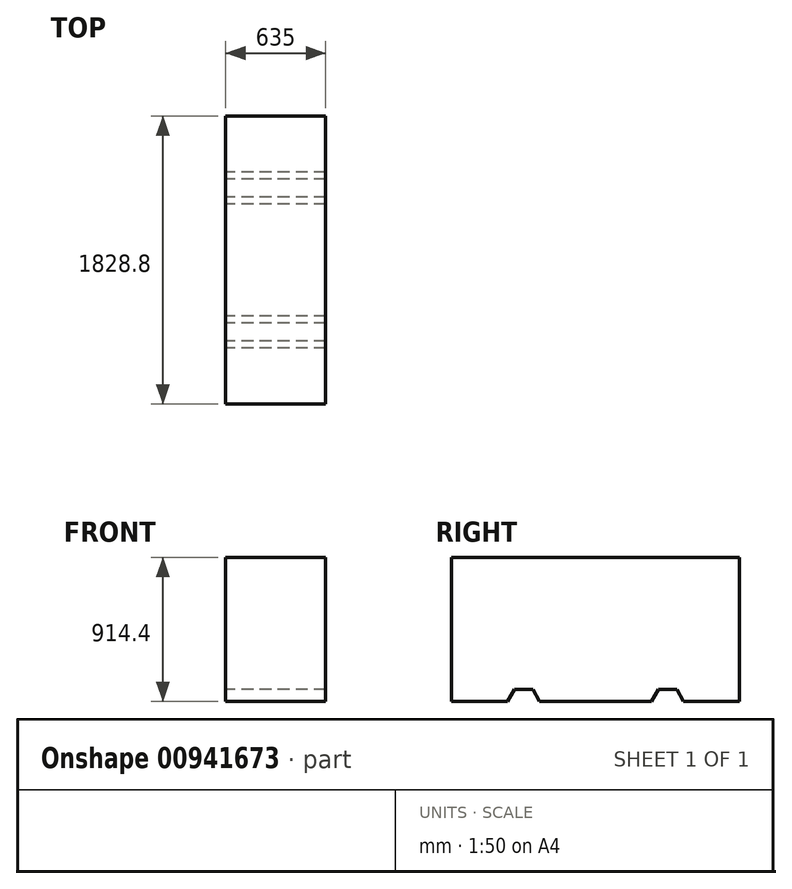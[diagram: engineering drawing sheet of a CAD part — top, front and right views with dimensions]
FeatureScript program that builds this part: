
annotation { "Feature Type Name" : "Feature", "Feature Type Description" : "" }
export const myFeature = defineFeature(function(context is Context, id is Id, definition is map)
    precondition{}
    {
        {
            var Q0;
            Q0=qCreatedBy(makeId("Right.planeOp"),FACE);
            var sketch = newSketch(context, id + "F0", { "sketchPlane" : qUnion([Q0])});
            skLineSegment(sketch, "E0.top", {"start": v(914.4, 457.2) * mm, "end": v(-914.4, 457.2) * mm});
            skLineSegment(sketch, "E0.left", {"start": v(914.4, -457.2) * mm, "end": v(914.4, 457.2) * mm});
            skLineSegment(sketch, "E0.right", {"start": v(-914.4, -457.2) * mm, "end": v(-914.4, 457.2) * mm});
            skPoint(sketch, "E0.middle", {"position": v(0, 0) * mm});
            skLineSegment(sketch, "E1", {"start": v(0, 607.57) * mm, "end": v(0, -605.26) * mm, "construction": true});
            skLineSegment(sketch, "E2", {"start": v(-457.2, 606.77) * mm, "end": v(-457.2, -606.07) * mm, "construction": true});
            skLineSegment(sketch, "E3", {"start": v(457.2, 704.09) * mm, "end": v(457.2, -508.75) * mm, "construction": true});
            skLineSegment(sketch, "E4", {"start": v(-914.4, -457.2) * mm, "end": v(-558.8, -457.2) * mm});
            skLineSegment(sketch, "E5", {"start": v(-558.8, -457.2) * mm, "end": v(-514.8, -381) * mm});
            skLineSegment(sketch, "E6", {"start": v(-514.8, -381) * mm, "end": v(-399.6, -381) * mm});
            skLineSegment(sketch, "E7", {"start": v(-399.6, -381) * mm, "end": v(-355.6, -457.2) * mm});
            skLineSegment(sketch, "E8", {"start": v(-355.6, -457.2) * mm, "end": v(355.6, -457.2) * mm});
            skLineSegment(sketch, "E9", {"start": v(355.6, -457.2) * mm, "end": v(399.6, -381) * mm});
            skLineSegment(sketch, "E10", {"start": v(399.6, -381) * mm, "end": v(514.8, -381) * mm});
            skLineSegment(sketch, "E11", {"start": v(514.8, -381) * mm, "end": v(558.8, -457.2) * mm});
            skLineSegment(sketch, "E12", {"start": v(558.8, -457.2) * mm, "end": v(914.4, -457.2) * mm});
            skSolve(sketch);
        }
        {
            var Q0;
            Q0=makeQuery(id+"F0.imprint","IMPRINT",FACE,{"disambiguationData":[TD([[makeQuery(id+"F0.imprint","IMPRINT",EDGE,{"derivedFrom":sQuery(id+"F0.wireOp",EDGE,"E0.top")}),1.0]])]});
            extrude(context, id + "F1", {"entities" : qUnion([Q0]), "depth" : 609.6 * mm, "offsetDistance" : 25.4 * mm});
        }
        {
            var Q0;
            Q0=makeQuery(id+"F1.opExtrude","SWEPT_FACE",FACE,{"disambiguationData":[OSD([sQuery(id+"F0.wireOp",EDGE,"E0.top")])]});
            shell(context, id + "F2", {"entities" : qUnion([Q0]), "thickness" : 76.2 * mm});
        }
        {
            var Q0;
            {var subQ3=sQuery(id+"F0.wireOp",EDGE,"E4");Q0=makeQuery(id+"F0.imprint","IMPRINT",FACE,{"disambiguationData":[TD([[makeQuery(id+"F0.imprint","IMPRINT",EDGE,{"derivedFrom":subQ3}),1.0]])]});}
            extrude(context, id + "F3", {"entities" : qUnion([Q0]), "operationType" : NewBodyOperationType.ADD, "depth" : 635 * mm, "offsetDistance" : 25.4 * mm});
        }
    });
